# Revit family: OASIS SHMD-6238
name_source: partatom
category: Plumbing Fixtures
revit_build: Autodesk Revit 2017 (Build: 20171027_0315(x64)
units: mm (PartAtom-declared; Revit-internal decimal feet)

## family parameters
Always vertical = Yes
Cut with Voids When Loaded = No
OmniClass Number = 23.45.05.14.21.11
OmniClass Title = Bath/Shower Units
Part Type = Normal
Room Calculation Point = No
Round Connector Dimension = Use Diameter
Shared = No
Work Plane-Based = No

## types (6) — shared parameters
BIM Model By = www.epoch-design.com
Bar_Horz_High_Center = 35"
Bar_Horz_Low_Center = 25"
Bar_Vert_Bottom = 53 1/2"
Cold Water Connector = Cold Water Connection
Color = <By Category>
Depth = 39"
Drain Clearance = 1/8"
Drain to back = 18 3/4"
Flange = 1 1/4"
Floor Height = 5/8"
Grab Bar Finish = <By Category>
Height = 76 1/4"
Hot Water Connector = Hot Water Connection
Interior Width = 60"
Manufacturer = OASIS
Sanitary Connector = Sanitary Connection
Sanitary Radius = 1 11/16"
Seat Finish = <By Category>
Seat_Remove = No
Stainless steel = <By Category>
Threshold = 3/4"
Threshold Depth = 3 3/4"
Type Comments = Shower
URL = www.oasisbath.com
Wall Thickness = 1"
Wall Thickness_Back = 1 1/4"
Width = 62"

## per-type parameters (varying)
| type | Bar_Horz_Back_36" | Bar_Horz_Back_48" | Bar_Horz_Left | Bar_Horz_Right | Bar_Vert | Model | Seat_Fold | Shower Rod |
| Base Model, 3SF, 3SM, FH, TLRF, TLRFDS, & TLVRF packages | No | No | No | No | No | SHMD-6232/(3SF. 3SM, FH, TLRF, TLRFDS,TLVRF) | No | No |
| 2 BAR package | Yes | No | Yes | No | No | SHMD-6232/2BAR | No | No |
| ADA-RI package | No | Yes | Yes | Yes | No | SHMD-6232/ADA-RI | No | Yes |
| ADA-TL package | Yes | No | Yes | No | No | SHMD-6232/ADA-TL | Yes | Yes |
| 3 BAR package | Yes | No | Yes | No | Yes | SHMD-6232/3BAR | No | No |
| ANS17 | Yes | No | Yes | No | Yes | SHMD-6232/ANS17 | Yes | Yes |

## geometry (parser evidence)
native form markers: Blend x2, Sweep x11
no freeform markers — native parametric forms only
